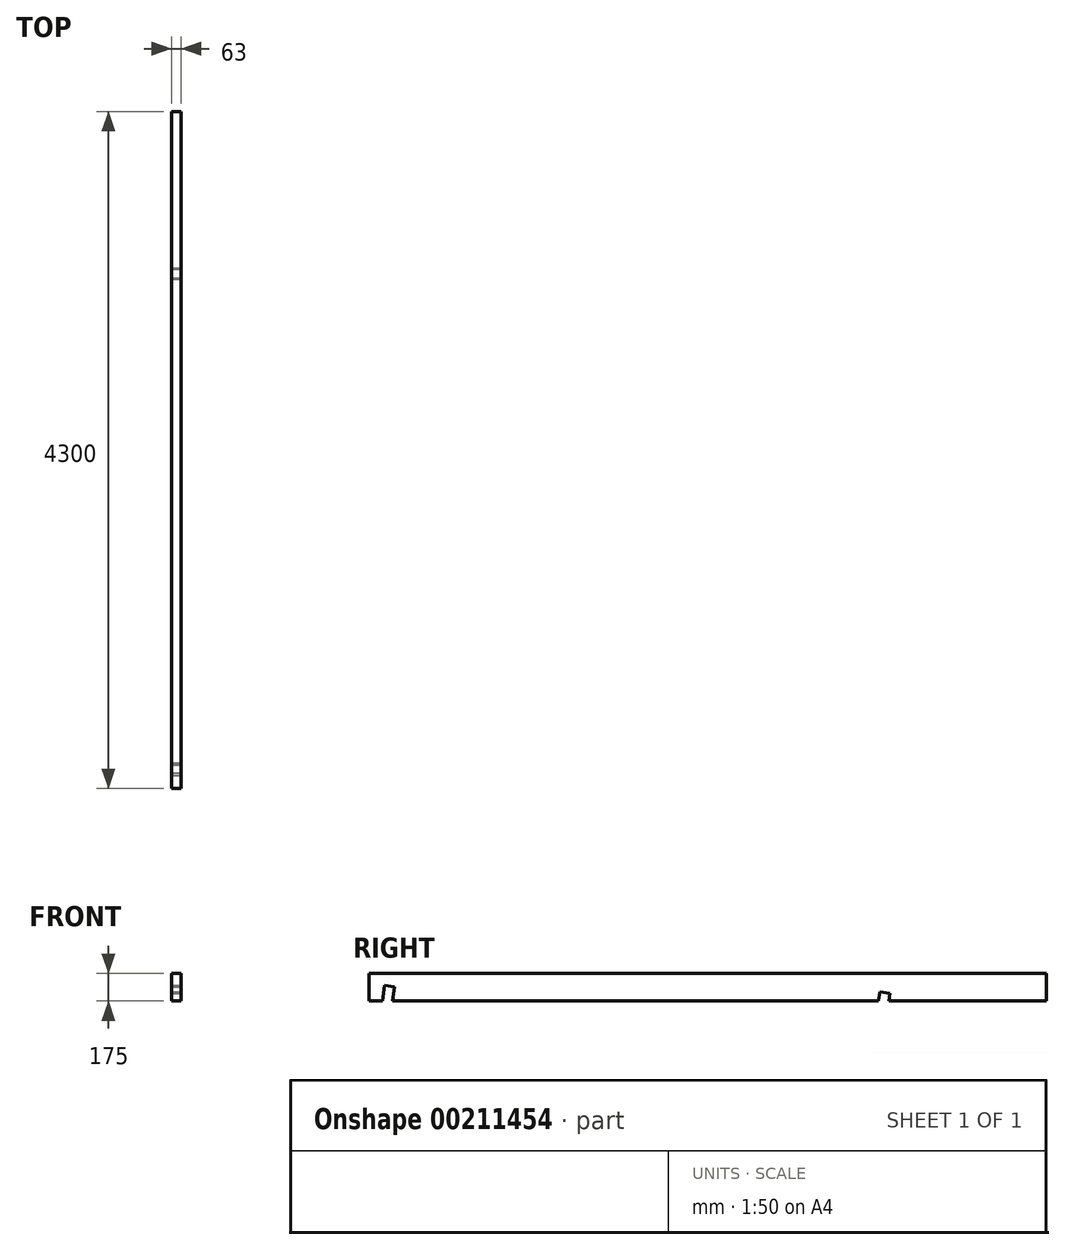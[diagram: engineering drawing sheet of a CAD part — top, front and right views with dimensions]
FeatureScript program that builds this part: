
annotation { "Feature Type Name" : "Feature", "Feature Type Description" : "" }
export const myFeature = defineFeature(function(context is Context, id is Id, definition is map)
    precondition{}
    {
        {
            var Q0;
            Q0=qCreatedBy(makeId("Front.planeOp"),FACE);
            var sketch = newSketch(context, id + "F0", { "sketchPlane" : qUnion([Q0])});
            skLineSegment(sketch, "E0.bottom", {"start": v(31.5, 87.5) * mm, "end": v(-31.5, 87.5) * mm});
            skLineSegment(sketch, "E0.top", {"start": v(31.5, -87.5) * mm, "end": v(-31.5, -87.5) * mm});
            skLineSegment(sketch, "E0.left", {"start": v(31.5, 87.5) * mm, "end": v(31.5, -87.5) * mm});
            skLineSegment(sketch, "E0.right", {"start": v(-31.5, 87.5) * mm, "end": v(-31.5, -87.5) * mm});
            skPoint(sketch, "E0.middle", {"position": v(0, 0) * mm});
            skSolve(sketch);
        }
        {
            var Q0;
            Q0=qSketchRegion(id+"F0",true);
            extrude(context, id + "F1", {"entities" : qUnion([Q0]), "depth" : 4300 * mm, "symmetric" : true});
        }
        {
            var Q0;
            Q0=makeQuery(id+"F1.opExtrude","SWEPT_FACE",FACE,{"disambiguationData":[OSD([sQuery(id+"F0.wireOp",EDGE,"E0.left")])]});
            var sketch = newSketch(context, id + "F2", { "sketchPlane" : qUnion([Q0])});
            skLineSegment(sketch, "E1", {"start": v(1150, -87.5) * mm, "end": v(1157.03, -37.5) * mm});
            skLineSegment(sketch, "E2", {"start": v(1157.03, -37.5) * mm, "end": v(1092.66, -28.45) * mm});
            skLineSegment(sketch, "E3", {"start": v(1092.66, -28.45) * mm, "end": v(1084.36, -87.5) * mm});
            skLineSegment(sketch, "E4", {"start": v(1084.36, -87.5) * mm, "end": v(1150, -87.5) * mm});
            skLineSegment(sketch, "E5", {"start": v(-2000.66, -87.5) * mm, "end": v(-1988.01, 2.5) * mm});
            skLineSegment(sketch, "E6", {"start": v(-1988.01, 2.5) * mm, "end": v(-2052.38, 11.55) * mm});
            skLineSegment(sketch, "E7", {"start": v(-2052.38, 11.55) * mm, "end": v(-2066.3, -87.5) * mm});
            skLineSegment(sketch, "E8", {"start": v(-2066.3, -87.5) * mm, "end": v(-2000.66, -87.5) * mm});
            skSolve(sketch);
        }
        {
            var Q0;
            Q0=qSketchRegion(id+"F2",true);
            extrude(context, id + "F3", {"entities" : qUnion([Q0]), "operationType" : NewBodyOperationType.REMOVE, "endBound" : BoundingType.UP_TO_NEXT, "oppositeDirection" : true, "depth" : 25 * mm});
        }
    });
